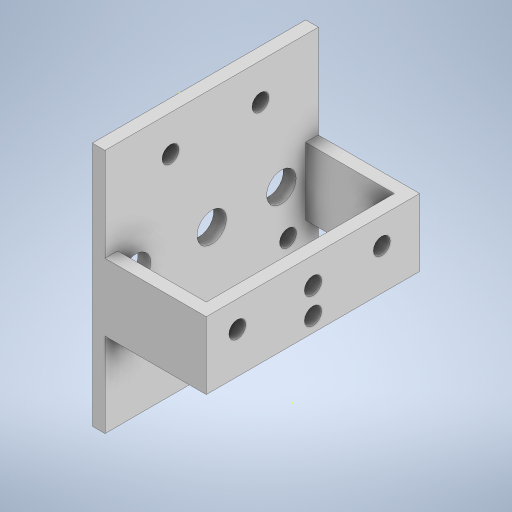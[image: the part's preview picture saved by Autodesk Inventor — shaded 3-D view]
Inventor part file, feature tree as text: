
AUTODESK INVENTOR PART (.ipt)
format: ipt  version: 2023 (Build 270158000, 158)  size: 863,744 bytes
history: native  units: mm
features: sketch x95, extrude x73, fillet x7
ambient origin geometry x8: Origin, YZ Plane, XZ Plane, XY Plane, X Axis, Y Axis, Z Axis, Center Point
bodies: Solid1 (feature_tree)
feature tree (175):
  extrude  "Extrusion1"  Depth=20.0mm
  extrude  "Extrusion2"  Depth=2.0mm
  extrude  "Extrusion3"  Depth=2.0mm
  sketch  "Sketch4"  dims[d8=20.0mm d9=0.0mm d10=4.0mm]
  sketch  "Sketch5"  dims[d11=3.0mm d12=0.0mm d13=5.0mm d14=0.0mm]
  extrude  "Extrusion4"  Depth=20.0mm
  extrude  "Extrusion5"  Depth=3.0mm TaperAngle=0.0deg
  extrude  "Extrusion6"  Depth=4.0mm
  sketch  "Sketch8"  dims[d22=30.0mm d23=0.0mm d24=4.0mm]
  extrude  "Extrusion7"  Depth=2.0mm TaperAngle=0.0deg
  extrude  "Extrusion8"  Depth=4.0mm
  extrude  "Extrusion9"  Depth=8.0mm
  extrude  "Extrusion10"  Depth=8.0mm TaperAngle=0.0deg
  sketch  "Sketch12"  dims[d35=30.0mm d36=0.0mm d37=23.0mm d38=0.0mm]
  sketch  "Sketch13"  dims[d39=4.0mm d40=25.0mm d41=0.0mm]
  extrude  "Extrusion11"  Depth=4.0mm
  extrude  "Extrusion12"  Depth=23.0mm TaperAngle=0.0deg
  extrude  "Extrusion13"  Depth=25.0mm TaperAngle=0.0deg
  sketch  "Sketch16"  dims[d47=25.0mm d48=0.0mm d49=2.0mm]
  sketch  "Sketch17"  dims[d50=25.0mm d51=0.0mm d52=25.0mm d53=0.0mm]
  extrude  "Extrusion14"  Depth=2.0mm TaperAngle=0.0deg
  sketch  "Sketch19"  dims[d57=0.018mm d58=31.0mm d59=0.0mm]
  extrude  "Extrusion15"  Depth=0.3mm
  sketch  "Sketch21"  dims[d62=3.0mm d63=0.0mm d64=3.0mm d65=0.0mm]
  sketch  "Sketch22"  dims[d66=2.0mm d67=2.0mm]
  extrude  "Extrusion16"  Depth=2.0mm
  extrude  "Extrusion17"  Depth=25.0mm TaperAngle=0.0deg
  extrude  "Extrusion18"  Depth=3.0mm TaperAngle=0.0deg
  extrude  "Extrusion19"  Depth=31.0mm TaperAngle=0.0deg
  extrude  "Extrusion20"  Depth=4.0mm
  extrude  "Extrusion21"  Depth=3.0mm TaperAngle=0.0deg
  sketch  "Sketch29"  dims[d95=4.0mm d96=4.0mm]
  extrude  "Extrusion22"  Depth=2.0mm
  sketch  "Sketch31"  dims[d100=3.0mm d101=0.0mm d102=1.0mm]
  sketch  "Sketch32"  dims[d103=3.0mm d104=0.0mm d105=1.0mm d106=0.0mm]
  extrude  "Extrusion23"  Depth=3.0mm TaperAngle=0.0deg
  extrude  "Extrusion24"  Depth=3.0mm TaperAngle=0.0deg
  fillet  "Fillet1"  Radius=25.0mm
  fillet  "Fillet2"  Radius=3.0mm
  sketch  "Sketch33"  dims[d107=1.0mm d108=0.0mm d109=10.0mm d110=0.0mm]
  extrude  "Extrusion25"  Depth=5.0mm TaperAngle=0.0deg
  sketch  "Sketch35"  dims[d114=2.0mm d115=4.0mm]
  extrude  "Extrusion26"  Depth=2.0mm TaperAngle=0.0deg
  sketch  "Sketch37"  dims[d119=5.5mm d120=10.0mm d121=0.0mm]
  extrude  "Extrusion27"  Depth=5.0mm TaperAngle=0.0deg
  extrude  "Extrusion28"  Depth=50.0mm TaperAngle=0.0deg
  sketch  "Sketch40"  dims[d127=70.0mm d128=0.0mm d129=2.0mm]
  extrude  "Extrusion29"  Depth=4.0mm
  extrude  "Extrusion30"  Depth=50.0mm TaperAngle=0.0deg
  extrude  "Extrusion31"  Depth=3.0mm
  sketch  "Sketch44"  dims[d139=20.0mm d140=0.0mm d141=2.0mm d142=10.0mm d143=0.0mm]
  sketch  "Sketch45"  dims[d144=40.0mm d145=0.0mm d146=40.0mm d147=0.0mm]
  extrude  "Extrusion32"  Depth=3.0mm TaperAngle=0.0deg
  sketch  "Sketch47"  dims[d151=21.0mm d152=0.0mm d153=3.0mm]
  extrude  "Extrusion33"  Depth=10.0mm TaperAngle=0.0deg
  extrude  "Extrusion34"  Depth=10.0mm TaperAngle=0.0deg
  extrude  "Extrusion35"  Depth=2.0mm
  extrude  "Extrusion36"  Depth=10.0mm
  extrude  "Extrusion37"  Depth=10.0mm TaperAngle=0.0deg
  extrude  "Extrusion38"  Depth=3.0mm
  extrude  "Extrusion39"  Depth=10.0mm
  extrude  "Extrusion40"  Depth=2.0mm
  extrude  "Extrusion41"  Depth=10.0mm TaperAngle=0.0deg
  extrude  "Extrusion42"  Depth=2.0mm
  sketch  "Sketch58"  dims[d190=10.0mm d191=0.0mm d192=10.0mm d193=0.0mm]
  extrude  "Extrusion43"  Depth=3.0mm TaperAngle=0.0deg
  extrude  "Extrusion44"  Depth=2.0mm
  fillet  "Fillet3"  Radius=10.0mm
  extrude  "Extrusion45"  Depth=40.0mm TaperAngle=0.0deg
  sketch  "Sketch62"
  extrude  "Extrusion46"  Depth=3.0mm
  extrude  "Extrusion47"  Depth=3.0mm
  extrude  "Extrusion48"  Depth=21.0mm TaperAngle=0.0deg
  fillet  "Fillet4"  Radius=4.0mm
  fillet  "Fillet5"  Radius=4.0mm
  extrude  "Extrusion49"  Depth=4.0mm
  sketch  "Sketch67"
  sketch  "Sketch68"
  sketch  "Sketch69"
  fillet  "Fillet6"  Radius=4.0mm
  extrude  "Extrusion50"  Depth=10.0mm TaperAngle=0.0deg
  extrude  "Extrusion51"  Depth=50.0mm TaperAngle=0.0deg
  extrude  "Extrusion52"  Depth=4.0mm
  fillet  "Fillet7"  Radius=50.0mm
  extrude  "Extrusion53"  Depth=7.0mm
  sketch  "Sketch74"
  extrude  "Extrusion54"  Depth=10.0mm TaperAngle=0.0deg
  extrude  "Extrusion55"  Depth=10.0mm
  extrude  "Extrusion56"  Depth=10.0mm TaperAngle=0.0deg
  extrude  "Extrusion57"  Depth=10.0mm TaperAngle=0.0deg
  extrude  "Extrusion58"  Depth=10.0mm TaperAngle=0.0deg
  extrude  "Extrusion59"  Depth=4.0mm
  extrude  "Extrusion60"  Depth=10.0mm
  extrude  "Extrusion61"  [1 undecoded]
  extrude  "Extrusion62"  [1 undecoded]
  extrude  "Extrusion63"  [1 undecoded]
  sketch  "Sketch85"
  extrude  "Extrusion64"  [1 undecoded]
  extrude  "Extrusion65"  [1 undecoded]
  extrude  "Extrusion66"  [1 undecoded]
  extrude  "Extrusion67"  [1 undecoded]
  extrude  "Extrusion68"  [1 undecoded]
  extrude  "Extrusion69"  [1 undecoded]
  extrude  "Extrusion70"  [1 undecoded]
  extrude  "Extrusion71"  [1 undecoded]
  sketch  "Sketch93"
  extrude  "Extrusion72"  [1 undecoded]
  extrude  "Extrusion73"  [1 undecoded]
  sketch  "Sketch1"  dims[d0=20.0mm d1=25.0mm]
  sketch  "Sketch2"  dims[d2=2.0mm d3=0.0mm d4=2.0mm]
  sketch  "Sketch3"  dims[d5=25.0mm d6=0.0mm d7=2.0mm]
  sketch  "Sketch6"  dims[d15=30.0mm d16=0.0mm d17=4.0mm]
  sketch  "Sketch7"  dims[d18=2.0mm d19=0.0mm d20=30.0mm d21=0.0mm]
  sketch  "Sketch9"  dims[d25=2.5mm d26=0.0mm d27=8.0mm]
  sketch  "Sketch10"  dims[d28=8.0mm d29=0.0mm d30=8.0mm d31=0.0mm]
  sketch  "Sketch11"  dims[d32=30.0mm d33=0.0mm d34=4.0mm]
  sketch  "Sketch14"  dims[d42=2.0mm d43=25.0mm d44=0.0mm]
  sketch  "Sketch15"  dims[d45=0.3mm d46=0.3mm]
  sketch  "Sketch18"  dims[d54=3.0mm d55=31.0mm d56=0.0mm]
  sketch  "Sketch20"  dims[d60=4.0mm d61=4.0mm]
  sketch  "Sketch23"  dims[d68=4.0mm d69=3.0mm d70=0.0mm]
  sketch  "Sketch24"  dims[d71=3.0mm d72=0.0mm d73=3.0mm d74=0.0mm d75=25.0mm d76=0.0mm d77=3.0mm d78=0.0mm]
  sketch  "Sketch25"  dims[d79=5.0mm d80=0.0mm d81=5.0mm d82=0.0mm]
  sketch  "Sketch26"  dims[d83=0.0mm d84=0.0mm d85=2.0mm d86=0.0mm]
  sketch  "Sketch27"  dims[d87=5.0mm d88=0.0mm d89=5.0mm d90=0.0mm]
  sketch  "Sketch28"  dims[d91=5.0mm d92=0.0mm d93=50.0mm d94=0.0mm]
  sketch  "Sketch30"  dims[d97=4.0mm d98=50.0mm d99=0.0mm]
  sketch  "Sketch34"  dims[d111=12.0mm d112=10.0mm d113=0.0mm]
  sketch  "Sketch36"  dims[d116=10.0mm d117=0.0mm d118=5.5mm]
  sketch  "Sketch38"  dims[d122=3.0mm d123=3.0mm]
  sketch  "Sketch39"  dims[d124=10.0mm d125=0.0mm d126=6.5mm]
  sketch  "Sketch41"  dims[d130=2.0mm d131=10.0mm d132=0.0mm]
  sketch  "Sketch42"  dims[d133=2.0mm d134=4.0mm]
  sketch  "Sketch43"  dims[d135=19.0mm d136=0.0mm d137=3.0mm d138=0.0mm]
  sketch  "Sketch46"  dims[d148=22.0mm d149=0.0mm d150=3.0mm]
  sketch  "Sketch48"  dims[d154=21.0mm d155=0.0mm d156=21.0mm d157=0.0mm d158=4.0mm d159=4.0mm]
  sketch  "Sketch49"  dims[d160=4.0mm d161=0.0mm d162=4.0mm d163=4.0mm d164=0.0mm]
  sketch  "Sketch50"  dims[d165=10.0mm d166=0.0mm d167=10.0mm d168=0.0mm]
  sketch  "Sketch51"  dims[d169=4.1mm d170=50.0mm d171=0.0mm]
  sketch  "Sketch52"  dims[d172=4.0mm d173=4.0mm d174=50.0mm d175=0.0mm]
  sketch  "Sketch53"  dims[d176=7.0mm d177=7.0mm]
  sketch  "Sketch54"  dims[d178=7.0mm d179=10.0mm d180=0.0mm]
  sketch  "Sketch55"  dims[d181=10.0mm d182=0.0mm d183=4.0mm]
  sketch  "Sketch56"  dims[d184=4.0mm d185=10.0mm d186=0.0mm]
  sketch  "Sketch57"  dims[d187=20.0mm d188=10.0mm d189=0.0mm]
  sketch  "Sketch59"  dims[d194=4.0mm d195=4.0mm]
  sketch  "Sketch60"  dims[d196=10.0mm d197=0.0mm d198=4.08mm]
  sketch  "Sketch61"  dims[d199=10.0mm d200=0.0mm]
  sketch  "Sketch63"
  sketch  "Sketch64"
  sketch  "Sketch65"
  sketch  "Sketch66"
  sketch  "Sketch70"
  sketch  "Sketch71"
  sketch  "Sketch72"
  sketch  "Sketch73"
  sketch  "Sketch75"
  sketch  "Sketch76"
  sketch  "Sketch77"
  sketch  "Sketch78"
  sketch  "Sketch79"
  sketch  "Sketch80"
  sketch  "Sketch81"
  sketch  "Sketch82"
  sketch  "Sketch83"
  sketch  "Sketch84"
  sketch  "Sketch86"
  sketch  "Sketch87"
  sketch  "Sketch88"
  sketch  "Sketch89"
  sketch  "Sketch90"
  sketch  "Sketch91"
  sketch  "Sketch92"
  sketch  "Sketch94"
  sketch  "Sketch95"
note: 13 required parameter values undecoded (feature->parameter linkage not recoverable at this tier; creation-order binding heuristic only, values carry confidence <= 0.55)
